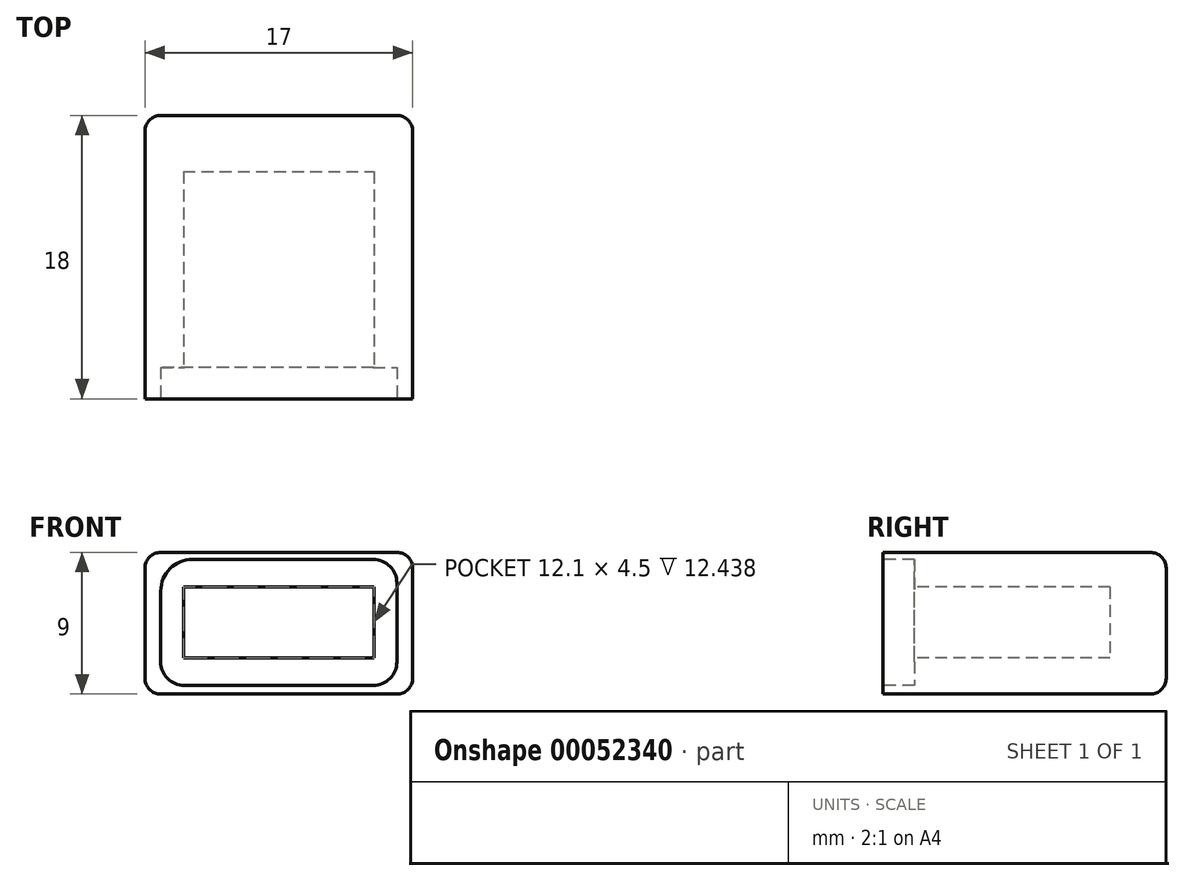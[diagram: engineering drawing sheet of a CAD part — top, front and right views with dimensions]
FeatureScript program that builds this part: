
annotation { "Feature Type Name" : "Feature", "Feature Type Description" : "" }
export const myFeature = defineFeature(function(context is Context, id is Id, definition is map)
    precondition{}
    {
        {
            var Q0;
            Q0=qCreatedBy(makeId("Front.planeOp"),FACE);
            var sketch = newSketch(context, id + "F0", { "sketchPlane" : qUnion([Q0])});
            skLineSegment(sketch, "E0.rect.top", {"start": v(7.5, 4.45) * mm, "end": v(-7.5, 4.45) * mm});
            skLineSegment(sketch, "E0.rect.left", {"start": v(8.5, -3.55) * mm, "end": v(8.5, 3.45) * mm});
            skLineSegment(sketch, "E0.rect.right", {"start": v(-8.5, -3.55) * mm, "end": v(-8.5, 3.45) * mm});
            skPoint(sketch, "E0.rect.middle", {"position": v(0, 0) * mm});
            skPoint(sketch, "E1.visualSharp", {"position": v(-8.5, 4.45) * mm});
            skArc(sketch, "E1.filletArc", {"start": v(-7.5, 4.45) * mm, "mid": v(-8.2, 4.15) * mm, "end": v(-8.5, 3.45) * mm});
            skPoint(sketch, "E2.visualSharp", {"position": v(8.5, 4.45) * mm});
            skArc(sketch, "E2.filletArc", {"start": v(8.5, 3.45) * mm, "mid": v(8.2, 4.15) * mm, "end": v(7.5, 4.45) * mm});
            skPoint(sketch, "E3.visualSharp", {"position": v(8.5, -4.45) * mm});
            skArc(sketch, "E3.filletArc", {"start": v(7.5, -4.55) * mm, "mid": v(8.2, -4.26) * mm, "end": v(8.5, -3.55) * mm});
            skLineSegment(sketch, "E4", {"start": v(7.5, -4.55) * mm, "end": v(-7.5, -4.55) * mm});
            skPoint(sketch, "E5.visualSharp", {"position": v(-8.5, -4.55) * mm});
            skArc(sketch, "E5.filletArc", {"start": v(-8.5, -3.55) * mm, "mid": v(-8.2, -4.26) * mm, "end": v(-7.5, -4.55) * mm});
            skSolve(sketch);
        }
        {
            var Q0;
            Q0=makeQuery(id+"F0.imprint","IMPRINT",FACE,{"disambiguationData":[TD([[makeQuery(id+"F0.imprint","IMPRINT",EDGE,{"derivedFrom":sQuery(id+"F0.wireOp",EDGE,"E0.rect.top")}),1.0]])]});
            extrude(context, id + "F1", {"entities" : qUnion([Q0]), "oppositeDirection" : true, "depth" : 18 * mm});
        }
        {
            var Q0;
            Q0=makeQuery(id+"F0.imprint","IMPRINT",FACE,{"disambiguationData":[TD([[makeQuery(id+"F0.imprint","IMPRINT",EDGE,{"derivedFrom":sQuery(id+"F0.wireOp",EDGE,"E0.rect.top")}),1.0]])]});
            var sketch = newSketch(context, id + "F2", { "sketchPlane" : qUnion([Q0])});
            skLineSegment(sketch, "E6.rect.bottom", {"start": v(-6.05, 2.25) * mm, "end": v(6.05, 2.25) * mm});
            skLineSegment(sketch, "E6.rect.top", {"start": v(-6.05, -2.25) * mm, "end": v(6.05, -2.25) * mm});
            skLineSegment(sketch, "E6.rect.left", {"start": v(-6.05, 2.25) * mm, "end": v(-6.05, -2.25) * mm});
            skLineSegment(sketch, "E6.rect.right", {"start": v(6.05, 2.25) * mm, "end": v(6.05, -2.25) * mm});
            skPoint(sketch, "E6.rect.middle", {"position": v(0, 0) * mm});
            skSolve(sketch);
        }
        {
            var Q0;
            Q0=qSketchRegion(id+"F2",true);
            var Q1;
            Q1=qSketchRegion(id+"F4",true);
            extrude(context, id + "F3", {"entities" : qUnion([Q0, Q1]), "operationType" : NewBodyOperationType.REMOVE, "oppositeDirection" : true, "depth" : 14.44 * mm});
        }
        {
            var Q0;
            Q0=makeQuery(id+"F0.imprint","IMPRINT",FACE,{"disambiguationData":[TD([[makeQuery(id+"F0.imprint","IMPRINT",EDGE,{"derivedFrom":sQuery(id+"F0.wireOp",EDGE,"E0.rect.top")}),1.0]])]});
            var sketch = newSketch(context, id + "F4", { "sketchPlane" : qUnion([Q0])});
            skLineSegment(sketch, "E7.rect.bottom", {"start": v(6, -4) * mm, "end": v(-6, -4) * mm});
            skLineSegment(sketch, "E7.rect.top", {"start": v(6, 4) * mm, "end": v(-5.5, 4) * mm});
            skLineSegment(sketch, "E7.rect.left", {"start": v(7.5, -2.5) * mm, "end": v(7.5, 2.5) * mm});
            skLineSegment(sketch, "E7.rect.right", {"start": v(-7.5, -2.5) * mm, "end": v(-7.5, 2) * mm});
            skPoint(sketch, "E7.rect.middle", {"position": v(0, 0) * mm});
            skPoint(sketch, "E8.visualSharp", {"position": v(-7.5, 4) * mm});
            skArc(sketch, "E8.filletArc", {"start": v(-5.5, 4) * mm, "mid": v(-6.91, 3.41) * mm, "end": v(-7.5, 2) * mm});
            skPoint(sketch, "E9.visualSharp", {"position": v(-7.5, -4) * mm});
            skArc(sketch, "E9.filletArc", {"start": v(-7.5, -2.5) * mm, "mid": v(-7.06, -3.56) * mm, "end": v(-6, -4) * mm});
            skPoint(sketch, "E10.visualSharp", {"position": v(7.5, -4) * mm});
            skArc(sketch, "E10.filletArc", {"start": v(6, -4) * mm, "mid": v(7.06, -3.56) * mm, "end": v(7.5, -2.5) * mm});
            skPoint(sketch, "E11.visualSharp", {"position": v(7.5, 4) * mm});
            skArc(sketch, "E11.filletArc", {"start": v(7.5, 2.5) * mm, "mid": v(7.06, 3.56) * mm, "end": v(6, 4) * mm});
            skSolve(sketch);
        }
        {
            var Q0;
            Q0=qSketchRegion(id+"F4",true);
            extrude(context, id + "F5", {"entities" : qUnion([Q0]), "operationType" : NewBodyOperationType.REMOVE, "oppositeDirection" : true, "depth" : 2 * mm});
        }
        {
            var Q0;
            Q0=makeQuery(id+"F1.opExtrude","CAP_FACE",FACE,{"disambiguationData":[OSD([sQuery(id+"F0.wireOp",EDGE,"E0.rect.top"),sQuery(id+"F0.wireOp",EDGE,"E0.rect.left"),sQuery(id+"F0.wireOp",EDGE,"E0.rect.right"),sQuery(id+"F0.wireOp",EDGE,"E1.filletArc"),sQuery(id+"F0.wireOp",EDGE,"E2.filletArc"),sQuery(id+"F0.wireOp",EDGE,"E3.filletArc"),sQuery(id+"F0.wireOp",EDGE,"E4"),sQuery(id+"F0.wireOp",EDGE,"E5.filletArc")])],"isStart":false});
            fillet(context, id + "F6", {"entities" : qUnion([Q0]), "radius" : 1 * mm, "tangentPropagation" : true, "allowEdgeOverflow" : false});
        }
    });
